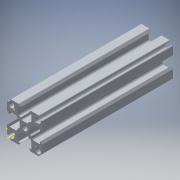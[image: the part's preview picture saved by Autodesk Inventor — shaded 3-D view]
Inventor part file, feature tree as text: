
AUTODESK INVENTOR PART (.ipt)
format: ipt  version: 2017 (Build 210142000, 142)  size: 317,952 bytes
history: native  units: in
note: dims shown in document units (in); Inventor stores cm internally (conversion verified against a paired STEP export)
features: sketch x2, extrude x1, fillet x1
ambient origin geometry x8: Origin, YZ Plane, XZ Plane, XY Plane, X Axis, Y Axis, Z Axis, Center Point
bodies: Solid1 (feature_tree)
feature tree (4):
  extrude  "Extrusion1"  [1 undecoded]
  sketch  "Sketch2"
  sketch  "Sketch1"  dims[d0=68.3in d1=0.0in]
  fillet  "Fillet10"  [1 undecoded]
note: 2 required parameter values undecoded (feature->parameter linkage not recoverable at this tier; creation-order binding heuristic only, values carry confidence <= 0.55)
